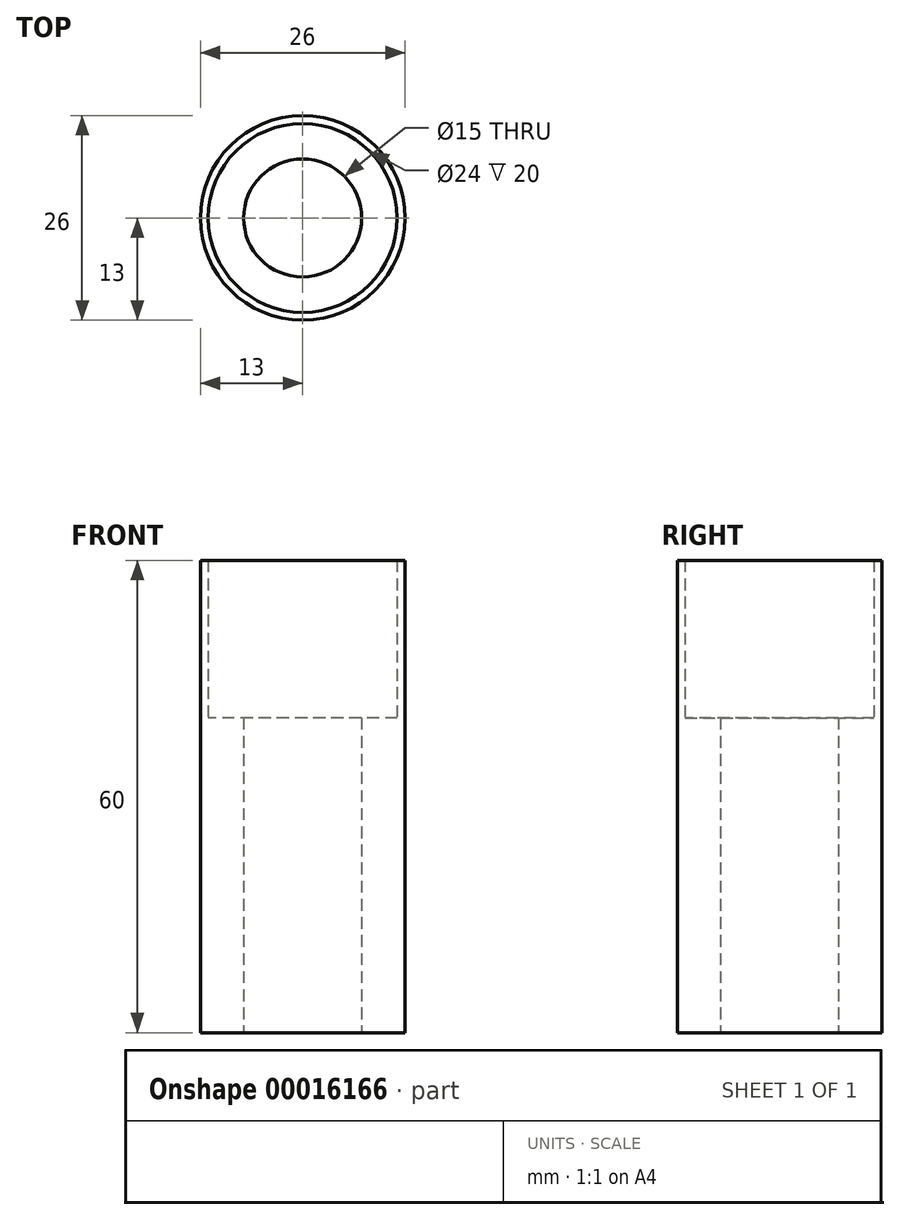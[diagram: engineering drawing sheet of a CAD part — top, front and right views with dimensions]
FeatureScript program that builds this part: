
annotation { "Feature Type Name" : "Feature", "Feature Type Description" : "" }
export const myFeature = defineFeature(function(context is Context, id is Id, definition is map)
    precondition{}
    {
        {
            var Q0;
            Q0=qCreatedBy(makeId("Top.planeOp"),FACE);
            var sketch = newSketch(context, id + "F0", { "sketchPlane" : qUnion([Q0])});
            skCircle(sketch, "E0", {"center": v(0, 0) * mm, "radius": 13 * mm});
            skCircle(sketch, "E1", {"center": v(0, 0) * mm, "radius": 7.5 * mm});
            skSolve(sketch);
        }
        {
            var Q0;
            Q0=qSketchRegion(id+"F0",true);
            extrude(context, id + "F1", {"entities" : qUnion([Q0]), "depth" : 40 * mm});
        }
        {
            var Q0;
            Q0=makeQuery(id+"F1.opExtrude","CAP_FACE",FACE,{"disambiguationData":[OSD([sQuery(id+"F0.wireOp",EDGE,"E0"),sQuery(id+"F0.wireOp",EDGE,"E1")])],"isStart":false});
            var sketch = newSketch(context, id + "F2", { "sketchPlane" : qUnion([Q0])});
            skCircle(sketch, "E2", {"center": v(0, 0) * mm, "radius": 13 * mm});
            skCircle(sketch, "E3", {"center": v(0, 0) * mm, "radius": 12 * mm});
            skSolve(sketch);
        }
        {
            var Q0;
            Q0 = qSketchRegion(id + "F2", true);
            extrude(context, id + "F3", {"entities" : qUnion([Q0]), "operationType" : NewBodyOperationType.ADD, "depth" : 20 * mm});
        }
    });
